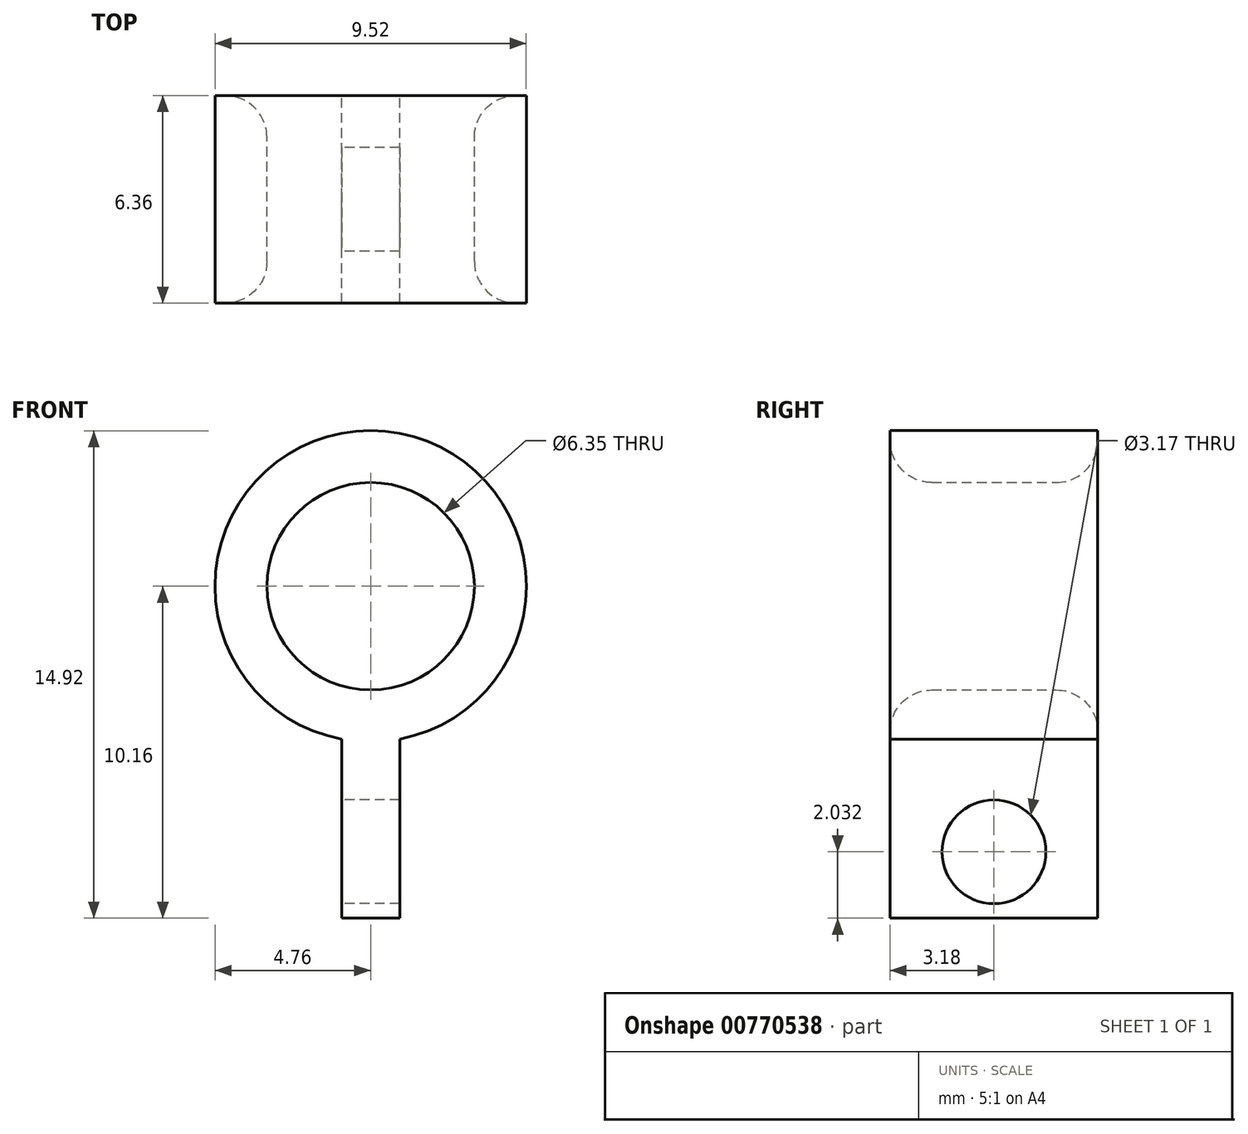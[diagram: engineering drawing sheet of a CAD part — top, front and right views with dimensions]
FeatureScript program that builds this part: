
annotation { "Feature Type Name" : "Feature", "Feature Type Description" : "" }
export const myFeature = defineFeature(function(context is Context, id is Id, definition is map)
    precondition{}
    {
        {
            var Q0;
            Q0=qCreatedBy(makeId("Front.planeOp"),FACE);
            var sketch = newSketch(context, id + "F0", { "sketchPlane" : qUnion([Q0])});
            skCircle(sketch, "E0", {"center": v(0, 0) * mm, "radius": 3.18 * mm});
            skCircle(sketch, "E1", {"center": v(0, 0) * mm, "radius": 4.76 * mm});
            skSolve(sketch);
        }
        {
            var Q0;
            Q0 = qSketchRegion(id + "F0", true);
            extrude(context, id + "F1", {"entities" : qUnion([Q0]), "endBound" : BoundingType.SYMMETRIC, "depth" : 6.35 * mm, "offsetDistance" : 25.4 * mm});
        }
        {
            var Q0;
            Q0=qCreatedBy(makeId("Right.planeOp"),FACE);
            var sketch = newSketch(context, id + "F2", { "sketchPlane" : qUnion([Q0])});
            skLineSegment(sketch, "E2.bottom", {"start": v(3.18, -3.8) * mm, "end": v(-3.18, -3.81) * mm});
            skLineSegment(sketch, "E2.top", {"start": v(3.17, -10.16) * mm, "end": v(-3.17, -10.16) * mm});
            skLineSegment(sketch, "E2.left", {"start": v(3.17, -3.81) * mm, "end": v(3.18, -10.16) * mm});
            skLineSegment(sketch, "E2.right", {"start": v(-3.18, -3.81) * mm, "end": v(-3.17, -10.16) * mm});
            skCircle(sketch, "E3", {"center": v(0, -8.13) * mm, "radius": 1.59 * mm});
            skPoint(sketch, "E4", {"position": v(0, -3.81) * mm});
            skSolve(sketch);
        }
        {
            var Q0;
            Q0 = qSketchRegion(id + "F2", true);
            extrude(context, id + "F3", {"entities" : qUnion([Q0]), "operationType" : NewBodyOperationType.ADD, "endBound" : BoundingType.SYMMETRIC, "depth" : 1.78 * mm, "offsetDistance" : 25.4 * mm});
        }
        {
            var Q0;
            Q0=makeQuery(id+"F1.opExtrude","CAP_EDGE",EDGE,{"disambiguationData":[OSD([sQuery(id+"F0.wireOp",EDGE,"E0")])],"isStart":false});
            var Q1;
            Q1=makeQuery(id+"F1.opExtrude","CAP_EDGE",EDGE,{"disambiguationData":[OSD([sQuery(id+"F0.wireOp",EDGE,"E0")])],"isStart":true});
            fillet(context, id + "F4", {"entities" : qUnion([Q0, Q1]), "radius" : 1.27 * mm, "tangentPropagation" : true, "allowEdgeOverflow" : false});
        }
    });
